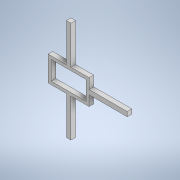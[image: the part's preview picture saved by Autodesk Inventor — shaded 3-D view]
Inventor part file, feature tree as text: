
AUTODESK INVENTOR PART (.ipt)
format: ipt  version: 2022 (Build 260153000, 153)  size: 122,880 bytes
history: native  units: mm
features: other x2, extrude x1, sketch x1
ambient origin geometry x8: Origin, YZ Plane, XZ Plane, XY Plane, X Axis, Y Axis, Z Axis, Center Point
bodies: Body1 (feature_tree)
feature tree (4):
  other  "FS90R.ipt"
  other  "ソリッド1"
  extrude  "押し出し1"  Depth=10.0mm
  sketch  "スケッチ2"
